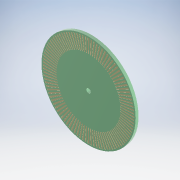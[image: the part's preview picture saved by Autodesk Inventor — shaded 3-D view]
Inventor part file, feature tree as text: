
AUTODESK INVENTOR PART (.ipt)
format: ipt  version: 2018.2 (Build 222227000, 227)  size: 872,448 bytes
history: native  units: mm
features: extrude x2, sketch x2, pattern_circular x1, plane x1, mirror x1
ambient origin geometry x8: Origin, YZ Plane, XZ Plane, XY Plane, X Axis, Y Axis, Z Axis, Center Point
bodies: Solid1 (feature_tree)
feature tree (7):
  extrude  "Extrusion1"  Depth=2.23mm
  extrude  "Extrusion2"  Depth=0.1mm
  pattern_circular  "Circular Pattern1"  [2 undecoded]
  plane  "Work Plane1"
  mirror  "Mirror1"
  sketch  "Sketch1"  dims[d0=48.0mm d1=2.23mm]
  sketch  "Sketch2"  dims[d2=1.5mm d3=0.0mm d4=0.7mm d5=7.0mm d6=0.75mm d7=0.1mm d8=0.0mm d9=1000.0mm d10=360.0deg d12=0.524678mm]
note: 2 required parameter values undecoded (feature->parameter linkage not recoverable at this tier; creation-order binding heuristic only, values carry confidence <= 0.55)
